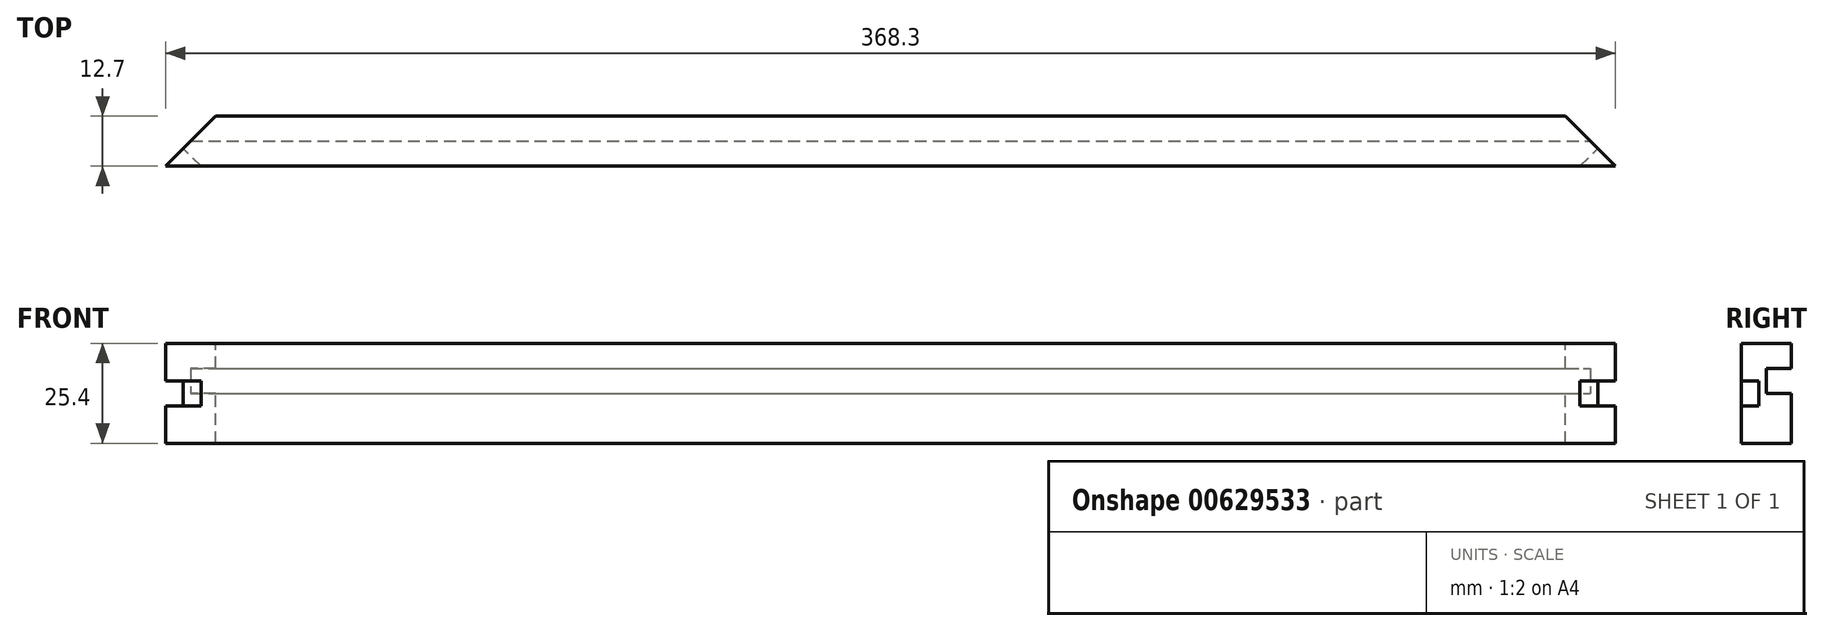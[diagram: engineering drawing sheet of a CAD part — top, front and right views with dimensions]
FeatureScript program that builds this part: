
annotation { "Feature Type Name" : "Feature", "Feature Type Description" : "" }
export const myFeature = defineFeature(function(context is Context, id is Id, definition is map)
    precondition{}
    {
        {
            var Q0;
            Q0=qCreatedBy(makeId("Front.planeOp"),FACE);
            var sketch = newSketch(context, id + "F0", { "sketchPlane" : qUnion([Q0])});
            skLineSegment(sketch, "E0.bottom", {"start": v(-184.15, 0) * mm, "end": v(184.15, 0) * mm});
            skLineSegment(sketch, "E0.top", {"start": v(-184.15, 25.4) * mm, "end": v(184.15, 25.4) * mm});
            skLineSegment(sketch, "E0.left", {"start": v(-184.15, 0) * mm, "end": v(-184.15, 25.4) * mm});
            skLineSegment(sketch, "E0.right", {"start": v(184.15, 0) * mm, "end": v(184.15, 25.4) * mm});
            skSolve(sketch);
        }
        {
            var Q0;
            Q0=makeQuery(id+"F0.imprint","IMPRINT",FACE,{"disambiguationData":[TD([[makeQuery(id+"F0.imprint","IMPRINT",EDGE,{"derivedFrom":sQuery(id+"F0.wireOp",EDGE,"E0.bottom")}),1.0]])]});
            extrude(context, id + "F1", {"entities" : qUnion([Q0]), "depth" : 12.7 * mm, "offsetDistance" : 25.4 * mm});
        }
        {
            var Q0;
            Q0=makeQuery(id+"F1.opExtrude","SWEPT_FACE",FACE,{"disambiguationData":[OSD([sQuery(id+"F0.wireOp",EDGE,"E0.right")])]});
            var sketch = newSketch(context, id + "F2", { "sketchPlane" : qUnion([Q0])});
            skLineSegment(sketch, "E1.bottom", {"start": v(0, 19.05) * mm, "end": v(-6.35, 19.05) * mm});
            skLineSegment(sketch, "E1.top", {"start": v(0, 12.7) * mm, "end": v(-6.35, 12.7) * mm});
            skLineSegment(sketch, "E1.left", {"start": v(0, 19.05) * mm, "end": v(0, 12.7) * mm});
            skLineSegment(sketch, "E1.right", {"start": v(-6.35, 19.05) * mm, "end": v(-6.35, 12.7) * mm});
            skSolve(sketch);
        }
        {
            var Q0;
            Q0 = qSketchRegion(id + "F2", true);
            extrude(context, id + "F3", {"entities" : qUnion([Q0]), "operationType" : NewBodyOperationType.REMOVE, "endBound" : BoundingType.THROUGH_ALL, "oppositeDirection" : true, "depth" : 25.4 * mm, "offsetDistance" : 25.4 * mm});
        }
        {
            var Q0;
            Q0=makeQuery(id+"F1.opExtrude","SWEPT_FACE",FACE,{"disambiguationData":[OSD([sQuery(id+"F0.wireOp",EDGE,"E0.top")])]});
            var sketch = newSketch(context, id + "F4", { "sketchPlane" : qUnion([Q0])});
            skLineSegment(sketch, "E2", {"start": v(-184.15, 0) * mm, "end": v(-171.45, 0) * mm});
            skLineSegment(sketch, "E3", {"start": v(-171.45, 0) * mm, "end": v(-184.15, -12.7) * mm});
            skLineSegment(sketch, "E4", {"start": v(-184.15, -12.7) * mm, "end": v(-184.15, 0) * mm});
            skLineSegment(sketch, "E5.MirrorCS", {"start": v(184.15, -12.7) * mm, "end": v(184.15, 0) * mm});
            skLineSegment(sketch, "E6.MirrorCS", {"start": v(171.45, 0) * mm, "end": v(184.15, -12.7) * mm});
            skLineSegment(sketch, "E7.MirrorCS", {"start": v(184.15, 0) * mm, "end": v(171.45, 0) * mm});
            skSolve(sketch);
        }
        {
            var Q0;
            Q0 = qSketchRegion(id + "F4", true);
            extrude(context, id + "F5", {"entities" : qUnion([Q0]), "operationType" : NewBodyOperationType.REMOVE, "endBound" : BoundingType.THROUGH_ALL, "oppositeDirection" : true, "depth" : 25.4 * mm, "offsetDistance" : 25.4 * mm});
        }
        {
            var Q0;
            Q0=makeQuery(id+"F5.boolean.opBoolean","COPY",FACE,{"derivedFrom":makeQuery(id+"F5.opExtrude","SWEPT_FACE",FACE,{"disambiguationData":[OSD([sQuery(id+"F4.wireOp",EDGE,"E6.MirrorCS")])]})});
            var sketch = newSketch(context, id + "F6", { "sketchPlane" : qUnion([Q0])});
            skLineSegment(sketch, "E8.bottom", {"start": v(-139.2, 15.88) * mm, "end": v(-132.84, 15.88) * mm});
            skLineSegment(sketch, "E8.top", {"start": v(-139.2, 9.53) * mm, "end": v(-132.84, 9.53) * mm});
            skLineSegment(sketch, "E8.left", {"start": v(-139.2, 15.88) * mm, "end": v(-139.2, 9.53) * mm});
            skLineSegment(sketch, "E8.right", {"start": v(-132.84, 15.88) * mm, "end": v(-132.84, 9.53) * mm});
            skSolve(sketch);
        }
        {
            var Q0;
            Q0 = qSketchRegion(id + "F6", true);
            extrude(context, id + "F7", {"entities" : qUnion([Q0]), "operationType" : NewBodyOperationType.REMOVE, "endBound" : BoundingType.THROUGH_ALL, "oppositeDirection" : true, "depth" : 25.4 * mm, "offsetDistance" : 25.4 * mm});
        }
        {
            var Q0;
            Q0=makeQuery(id+"F5.boolean.opBoolean","COPY",FACE,{"derivedFrom":makeQuery(id+"F5.opExtrude","SWEPT_FACE",FACE,{"disambiguationData":[OSD([sQuery(id+"F4.wireOp",EDGE,"E3")])]})});
            var sketch = newSketch(context, id + "F8", { "sketchPlane" : qUnion([Q0])});
            skLineSegment(sketch, "E9.bottom", {"start": v(139.2, 15.88) * mm, "end": v(132.84, 15.88) * mm});
            skLineSegment(sketch, "E9.top", {"start": v(139.2, 9.52) * mm, "end": v(132.84, 9.52) * mm});
            skLineSegment(sketch, "E9.left", {"start": v(139.2, 15.88) * mm, "end": v(139.2, 9.52) * mm});
            skLineSegment(sketch, "E9.right", {"start": v(132.84, 15.88) * mm, "end": v(132.84, 9.52) * mm});
            skSolve(sketch);
        }
        {
            var Q0;
            Q0 = qSketchRegion(id + "F8", true);
            extrude(context, id + "F9", {"entities" : qUnion([Q0]), "operationType" : NewBodyOperationType.REMOVE, "endBound" : BoundingType.THROUGH_ALL, "oppositeDirection" : true, "depth" : 25.4 * mm, "offsetDistance" : 25.4 * mm});
        }
    });
